# Revit family: AC2E_DXSX
name_source: partatom
category: Attrezzature speciali
revit_build: Autodesk Revit 2017 (Build: 20160225_1515(x64)
units: mm (PartAtom-declared; Revit-internal decimal feet)

## family parameters
Basato su piano di lavoro = No
Condiviso = No
Punto di calcolo locali = No
Quota connettore circolare = Usa raggio
Sempre verticale = Sì
Taglio con vuoti quando caricato = No
Tipo di parte = Normale

## types (8) — shared parameters
Capacity ecorinse tank = 14.0 L
Capacity washing tank = 80.0 L
Ecorinse pump = 0.48 kW
First speed = 0.0145 m/s
Flow Rinsing = 2.2 l/min
Gearmotor = 0.18 kW
Height of the machine = 1450 mm
Height with RC = 2040 mm
Height with open doors = 2000 mm
Length of TECH Splash Shield = 200 mm
Length of drying = 600 mm
Length of the first module = 1150 mm
Length of the second module = 400 mm
Maximum flow Rinsing = 3.3 l/min
Modello = AC2
Powered Boiler = No
Production with the first speed (cest/h) = 105
Production with the second speed (cest/h) = 140
RCD = No
RCD pump = 0 kW
Second speed = 0.0195 m/s
Steam Inlet = 2"
Steam Outlet = 1"
Tanks drain diameter = 50 mm
Total capacity = 94.0 L
Washing pump = 1.24 kW
Water inlet = 1"
zero-valued in all types: Costo

## per-type parameters (varying)
| type | Depth | Drying Tunnel | Electric | Exchange surface RC | Fan RC | Fan drying | Installed power | Maximum height | RC | Resistance drying | Resistance rinsing | Resistance washing | Steam | Total depth | Total length | Total steam heating kg/h |
| AC2E D/S AS RC ELECTRIC EXECUTION | 790 mm | Sì | Sì | 21.00 m² | 0.05 kW | 0.42 kW | 31.37 kW | 2040 mm | Sì | 6 kW | 11 kW | 12 kW | No | 840 mm | 2350 mm | 0 |
| AC2E D/S AS ELECTRIC EXECUTION | 790 mm | Sì | Sì | 0.00 m² | 0 kW | 0.42 kW | 28.32 kW | 2000 mm | No | 6 kW | 8 kW | 12 kW | No | 840 mm | 2350 mm | 0 |
| AC2E D/S RC ELECTRIC EXECUTION | 790 mm | No | Sì | 21.00 m² | 0.05 kW | 0 kW | 24.95 kW | 2040 mm | Sì | 0 kW | 11 kW | 12 kW | No | 840 mm | 1750 mm | 0 |
| AC2E D/S ELECTRIC EXECUTION | 790 mm | No | Sì | 0.00 m² | 0 kW | 0 kW | 21.9 kW | 2000 mm | No | 0 kW | 8 kW | 12 kW | No | 840 mm | 1750 mm | 0 |
| AC2E D/S RC STEAM EXECUTION | 820 mm | No | No | 21.00 m² | 0.05 kW | 0 kW | 1.95 kW | 2040 mm | Sì | 0 kW | 0 kW | 0 kW | Sì | 870 mm | 1750 mm | 39.7 |
| AC2E D/S AS STEAM EXECUTION | 820 mm | Sì | No | 0.00 m² | 0 kW | 0.42 kW | 2.32 kW | 2000 mm | No | 0 kW | 0 kW | 0 kW | Sì | 870 mm | 2350 mm | 44.8 |
| AC2E D/S AS RC STEAM EXECUTION | 790 mm | Sì | Sì | 21.00 m² | 0.05 kW | 0.42 kW | 31.37 kW | 2040 mm | Sì | 6 kW | 11 kW | 12 kW | No | 840 mm | 2350 mm | 0 |
| AC2E D/S STEAM EXECUTION | 820 mm | No | No | 0.00 m² | 0 kW | 0 kW | 1.9 kW | 2000 mm | No | 0 kW | 0 kW | 0 kW | Sì | 870 mm | 1750 mm | 34.5 |
